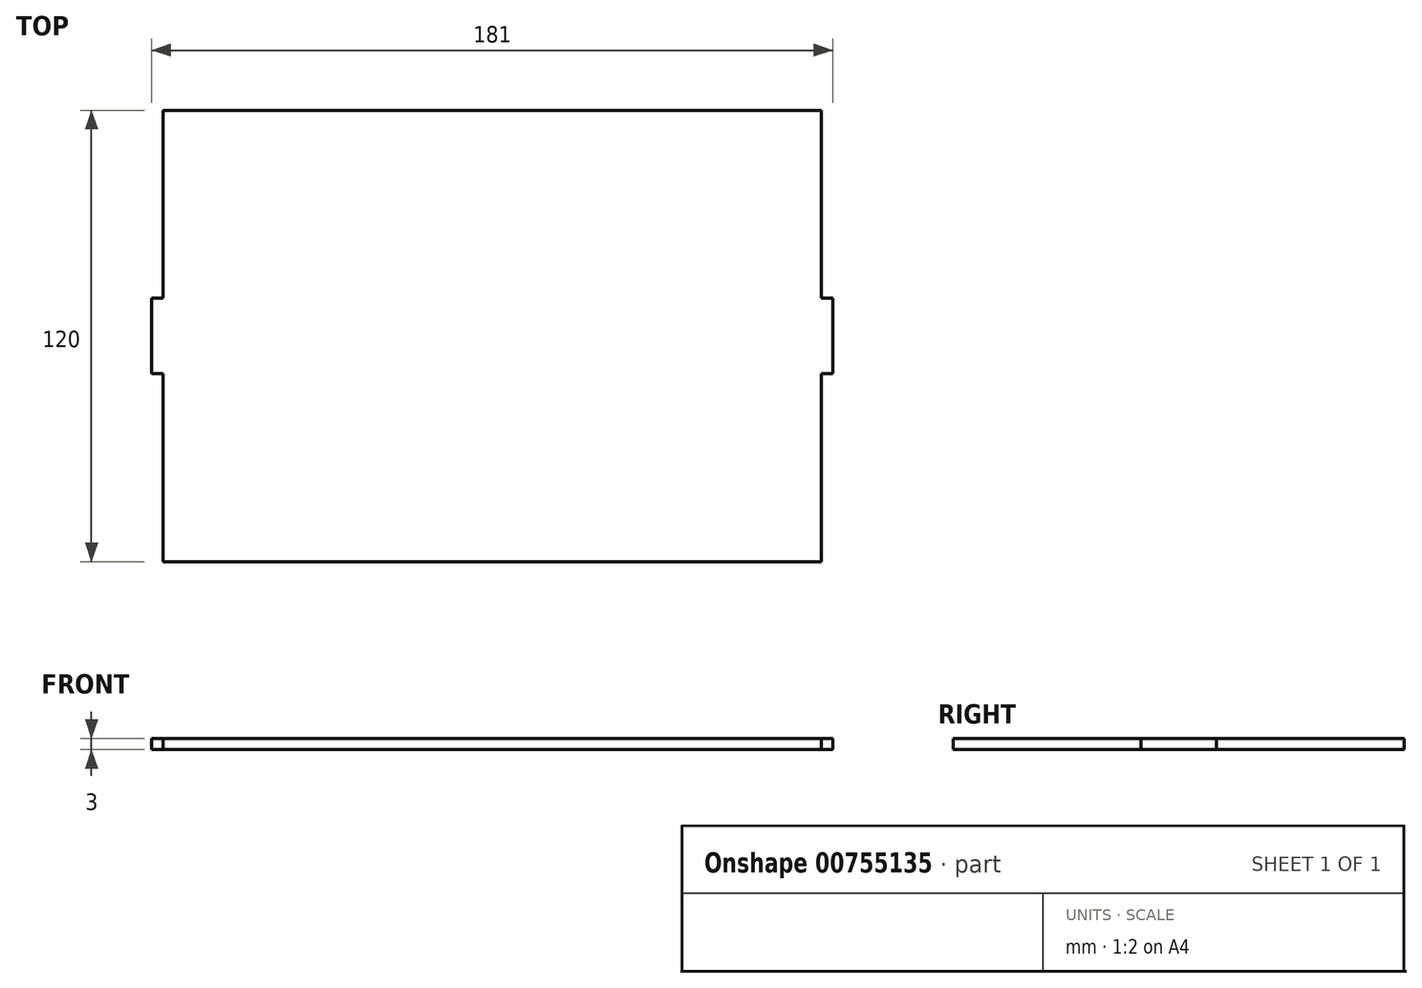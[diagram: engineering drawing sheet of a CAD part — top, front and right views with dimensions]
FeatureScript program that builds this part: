
annotation { "Feature Type Name" : "Feature", "Feature Type Description" : "" }
export const myFeature = defineFeature(function(context is Context, id is Id, definition is map)
    precondition{}
    {
        {
            var Q0;
            Q0=qCreatedBy(makeId("Top.planeOp"),FACE);
            var sketch = newSketch(context, id + "F0", { "sketchPlane" : qUnion([Q0])});
            skLineSegment(sketch, "E0.bottom", {"start": v(0, 0) * mm, "end": v(175, 0) * mm});
            skLineSegment(sketch, "E0.top", {"start": v(0, 120) * mm, "end": v(175, 120) * mm});
            skLineSegment(sketch, "E0.left", {"start": v(0, 0) * mm, "end": v(0, 120) * mm});
            skLineSegment(sketch, "E0.right", {"start": v(175, 0) * mm, "end": v(175, 120) * mm});
            skLineSegment(sketch, "E1.bottom", {"start": v(175, 50) * mm, "end": v(178, 50) * mm});
            skLineSegment(sketch, "E1.top", {"start": v(175, 70) * mm, "end": v(178, 70) * mm});
            skLineSegment(sketch, "E1.left", {"start": v(175, 50) * mm, "end": v(175, 70) * mm});
            skLineSegment(sketch, "E1.right", {"start": v(178, 50) * mm, "end": v(178, 70) * mm});
            skLineSegment(sketch, "E2.bottom", {"start": v(0, 50) * mm, "end": v(-3, 50) * mm});
            skLineSegment(sketch, "E2.top", {"start": v(0, 70) * mm, "end": v(-3, 70) * mm});
            skLineSegment(sketch, "E2.left", {"start": v(0, 50) * mm, "end": v(0, 70) * mm});
            skLineSegment(sketch, "E2.right", {"start": v(-3, 50) * mm, "end": v(-3, 70) * mm});
            skSolve(sketch);
        }
        {
            var Q0;
            Q0 = qSketchRegion(id + "F0", true);
            extrude(context, id + "F1", {"entities" : qUnion([Q0]), "depth" : 3 * mm, "offsetDistance" : 25 * mm});
        }
    });
